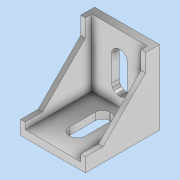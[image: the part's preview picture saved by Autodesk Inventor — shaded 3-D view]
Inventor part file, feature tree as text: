
AUTODESK INVENTOR PART (.ipt)
format: ipt  version: 2021 (Build 250183000, 183)  size: 193,024 bytes
history: native  units: in
note: dims shown in document units (in); Inventor stores cm internally (conversion verified against a paired STEP export)
features: extrude x4, sketch x4, projected_geometry x3, mirror x1, plane x1
ambient origin geometry x8: Origin, YZ Plane, XZ Plane, XY Plane, X Axis, Y Axis, Z Axis, Center Point
bodies: Solid1 (feature_tree)
feature tree (13):
  extrude  "Extrusion1"  Depth=0.7874in
  extrude  "Extrusion2"  Depth=1.5748in
  extrude  "Extrusion3"  Depth=0.0984in
  extrude  "Extrusion4"  Depth=0.0984in
  mirror  "Mirror1"
  sketch  "Sketch1"  dims[d2=0.689in d3=0.7874in]
  sketch  "Sketch2"  dims[d4=1.378in d5=1.5748in]
  projected_geometry  "Projected Loop1"
  sketch  "Sketch3"  dims[d6=1.378in d7=0.0984in]
  projected_geometry  "Projected Loop2"
  sketch  "Sketch4"  dims[d8=0.4331in d9=0.4331in d10=0.1673in d11=0.3346in d12=0.1575in d13=0.1575in d14=0.0in d15=0.1575in d16=1.4173in d17=0.0in d18=0.4331in d19=0.4331in d20=0.1673in d21=0.8661in d22=0.3346in d23=0.1575in d24=0.1575in d25=0.0in d26=0.1378in d27=0.1378in d28=0.374in d29=0.374in d30=0.0984in d31=0.0in]
  projected_geometry  "Projected Loop3"
  plane  "Work Plane1"
